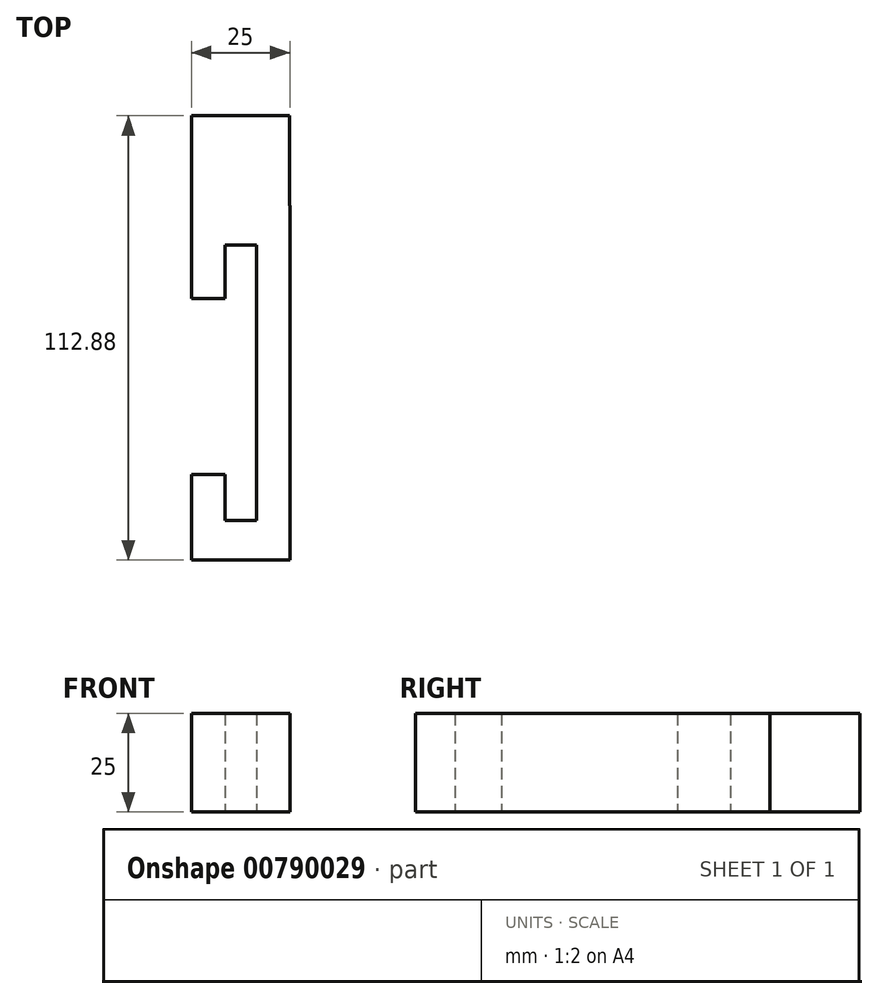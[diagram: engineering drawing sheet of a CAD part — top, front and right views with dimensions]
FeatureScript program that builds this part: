
annotation { "Feature Type Name" : "Feature", "Feature Type Description" : "" }
export const myFeature = defineFeature(function(context is Context, id is Id, definition is map)
    precondition{}
    {
        {
            var Q0;
            Q0=qCreatedBy(makeId("Top.planeOp"),FACE);
            var sketch = newSketch(context, id + "F0", { "sketchPlane" : qUnion([Q0])});
            skLineSegment(sketch, "E0.bottom", {"start": v(12.4, 45) * mm, "end": v(12.5, 45) * mm});
            skLineSegment(sketch, "E0.top", {"start": v(-12.5, -45) * mm, "end": v(12.5, -45) * mm});
            skLineSegment(sketch, "E0.left", {"start": v(-12.5, 45) * mm, "end": v(-12.5, 21.44) * mm});
            skLineSegment(sketch, "E0.right", {"start": v(12.5, 45) * mm, "end": v(12.5, -45) * mm});
            skPoint(sketch, "E0.middle", {"position": v(0, 0) * mm});
            skLineSegment(sketch, "E1.bottom", {"start": v(-4, 35) * mm, "end": v(4, 35) * mm});
            skLineSegment(sketch, "E1.top", {"start": v(-4, -35) * mm, "end": v(4, -35) * mm});
            skLineSegment(sketch, "E1.left", {"start": v(-4, 35) * mm, "end": v(-4, 21.44) * mm});
            skLineSegment(sketch, "E1.right", {"start": v(4, 35) * mm, "end": v(4, -35) * mm});
            skLineSegment(sketch, "E2", {"start": v(-4, 21.44) * mm, "end": v(-12.5, 21.44) * mm});
            skLineSegment(sketch, "E3", {"start": v(-4, -23.24) * mm, "end": v(-12.5, -23.24) * mm});
            skLineSegment(sketch, "E4.trimOffspring", {"start": v(-12.5, -23.24) * mm, "end": v(-12.5, -45) * mm});
            skLineSegment(sketch, "E5.trimOffspring", {"start": v(-4, -23.24) * mm, "end": v(-4, -35) * mm});
            skLineSegment(sketch, "E6.top", {"start": v(-12.5, 67.88) * mm, "end": v(12.4, 67.88) * mm});
            skLineSegment(sketch, "E6.left", {"start": v(-12.5, 45) * mm, "end": v(-12.5, 67.88) * mm});
            skLineSegment(sketch, "E6.right", {"start": v(12.4, 45) * mm, "end": v(12.4, 67.88) * mm});
            skSolve(sketch);
        }
        {
            var Q0;
            Q0=makeQuery(id+"F0.imprint","IMPRINT",FACE,{"disambiguationData":[TD([[makeQuery(id+"F0.imprint","IMPRINT",EDGE,{"derivedFrom":sQuery(id+"F0.wireOp",EDGE,"E0.bottom")}),-1.0]])]});
            extrude(context, id + "F1", {"entities" : qUnion([Q0]), "endBound" : BoundingType.SYMMETRIC, "depth" : 25 * mm, "offsetDistance" : 25 * mm});
        }
    });
